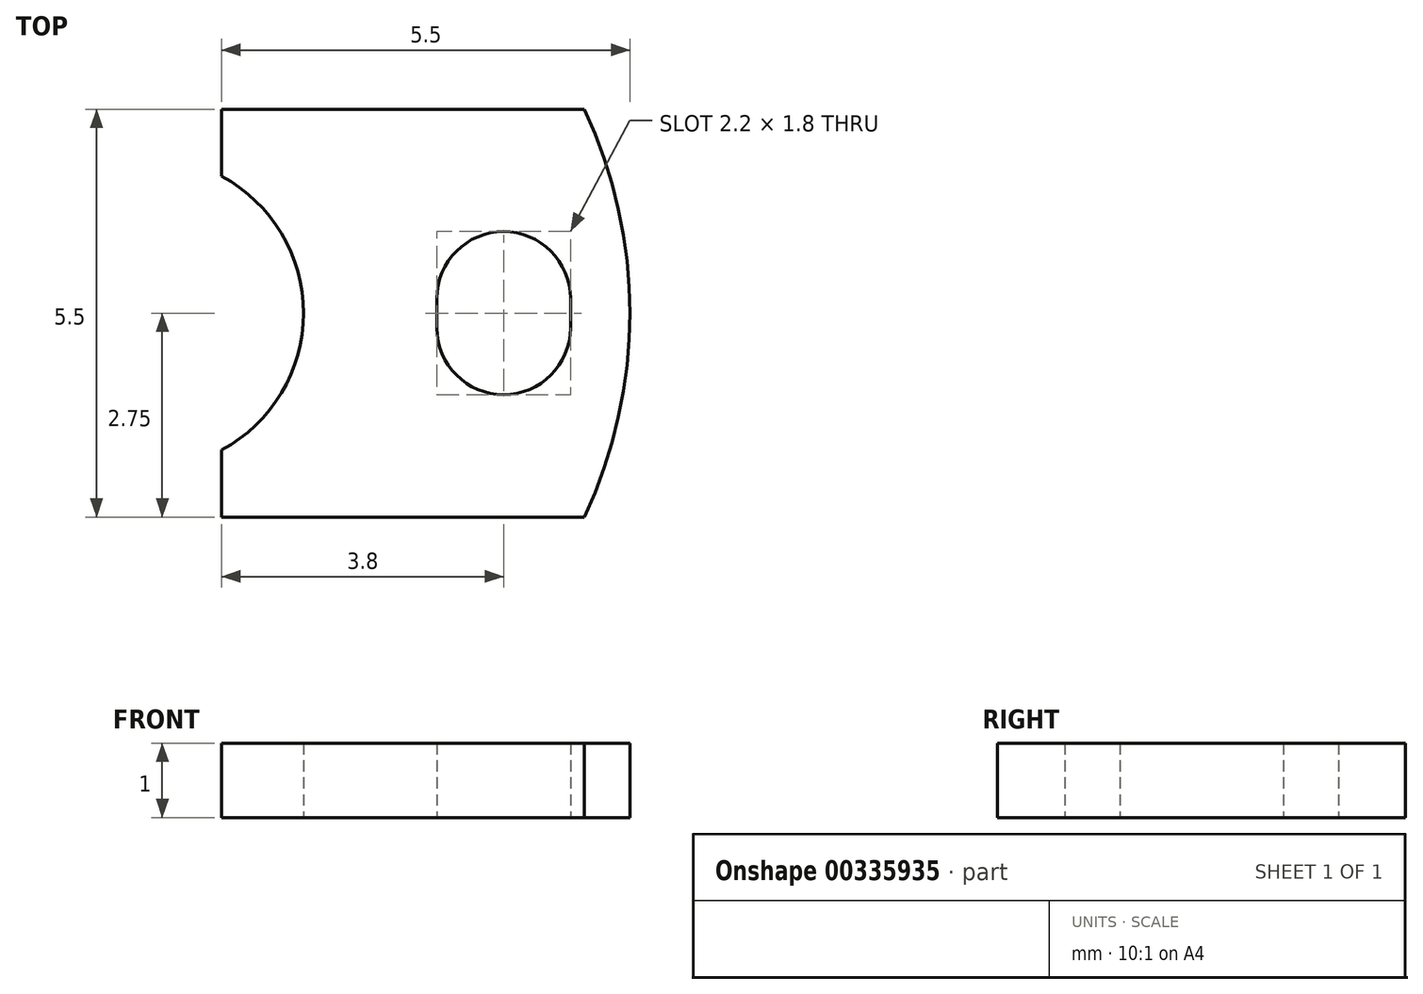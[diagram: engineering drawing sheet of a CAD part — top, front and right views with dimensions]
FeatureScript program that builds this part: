
annotation { "Feature Type Name" : "Feature", "Feature Type Description" : "" }
export const myFeature = defineFeature(function(context is Context, id is Id, definition is map)
    precondition{}
    {
        {
            var Q0;
            Q0=qCreatedBy(makeId("Top.planeOp"),FACE);
            var sketch = newSketch(context, id + "F0", { "sketchPlane" : qUnion([Q0])});
            skArc(sketch, "E0", {"start": v(1, -1.85) * mm, "mid": v(2.1, 0) * mm, "end": v(1, 1.85) * mm});
            skArc(sketch, "E1", {"start": v(5.89, -2.75) * mm, "mid": v(6.5, 0) * mm, "end": v(5.89, 2.75) * mm});
            skLineSegment(sketch, "E2", {"start": v(5.89, 2.75) * mm, "end": v(1, 2.75) * mm});
            skLineSegment(sketch, "E3", {"start": v(1, 2.75) * mm, "end": v(1, 1.85) * mm});
            skLineSegment(sketch, "E4", {"start": v(1, -1.85) * mm, "end": v(1, -2.75) * mm});
            skLineSegment(sketch, "E5", {"start": v(1, -2.75) * mm, "end": v(5.89, -2.75) * mm});
            skPoint(sketch, "E6", {"position": v(6.5, 0) * mm});
            skLineSegment(sketch, "E7", {"start": v(3.9, 0.2) * mm, "end": v(3.9, -0.2) * mm});
            skLineSegment(sketch, "E8", {"start": v(3.9, 0.2) * mm, "end": v(5.7, 0.2) * mm, "construction": true});
            skLineSegment(sketch, "E9", {"start": v(3.9, -0.2) * mm, "end": v(5.7, -0.2) * mm, "construction": true});
            skLineSegment(sketch, "E10", {"start": v(5.7, 0.2) * mm, "end": v(5.7, -0.2) * mm});
            skArc(sketch, "E11", {"start": v(3.9, 0.2) * mm, "mid": v(4.8, 1.1) * mm, "end": v(5.7, 0.2) * mm});
            skArc(sketch, "E12", {"start": v(3.9, -0.2) * mm, "mid": v(4.8, -1.1) * mm, "end": v(5.7, -0.2) * mm});
            skPoint(sketch, "E13", {"position": v(4.8, 1.1) * mm});
            skPoint(sketch, "E14", {"position": v(4.8, -1.1) * mm});
            skLineSegment(sketch, "E15", {"start": v(4.8, 1.1) * mm, "end": v(4.8, -1.1) * mm, "construction": true});
            skPoint(sketch, "E16", {"position": v(4.8, 0) * mm});
            skSolve(sketch);
        }
        {
            var Q0;
            Q0 = qSketchRegion(id + "F0", true);
            extrude(context, id + "F1", {"entities" : qUnion([Q0]), "depth" : 1 * mm});
        }
    });
